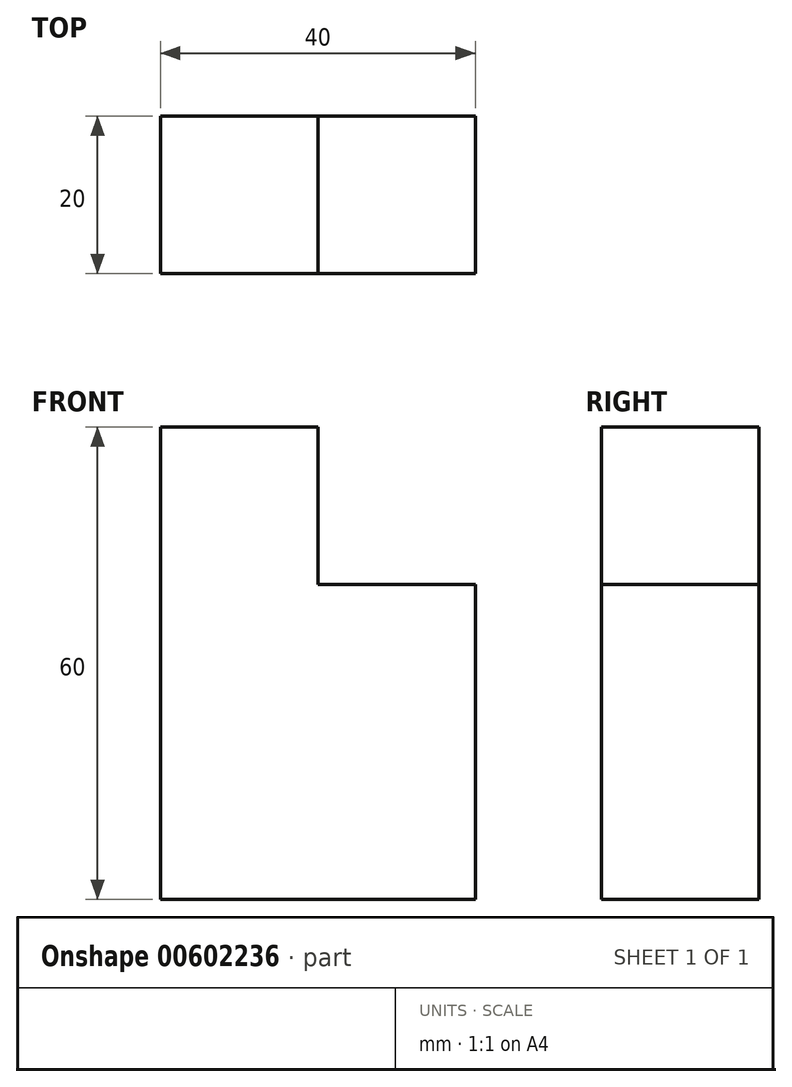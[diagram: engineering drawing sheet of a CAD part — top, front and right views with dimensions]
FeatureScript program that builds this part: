
annotation { "Feature Type Name" : "Feature", "Feature Type Description" : "" }
export const myFeature = defineFeature(function(context is Context, id is Id, definition is map)
    precondition{}
    {
        {
            var Q0;
            Q0=qCreatedBy(makeId("Front.planeOp"),FACE);
            var sketch = newSketch(context, id + "F0", { "sketchPlane" : qUnion([Q0])});
            skLineSegment(sketch, "E0", {"start": v(-55.5, 45.58) * mm, "end": v(-35.5, 45.58) * mm});
            skLineSegment(sketch, "E1", {"start": v(-35.5, 45.58) * mm, "end": v(-35.5, 25.58) * mm});
            skLineSegment(sketch, "E2", {"start": v(-35.5, 25.58) * mm, "end": v(-15.5, 25.58) * mm});
            skLineSegment(sketch, "E3", {"start": v(-15.5, 25.58) * mm, "end": v(-15.5, -14.42) * mm});
            skLineSegment(sketch, "E4", {"start": v(-15.5, -14.42) * mm, "end": v(-55.5, -14.42) * mm});
            skLineSegment(sketch, "E5", {"start": v(-55.5, -14.42) * mm, "end": v(-55.5, 45.58) * mm});
            skSolve(sketch);
        }
        {
            var Q0;
            Q0 = qSketchRegion(id + "F0", true);
            extrude(context, id + "F1", {"entities" : qUnion([Q0]), "depth" : 20 * mm, "offsetDistance" : 25 * mm});
        }
    });
